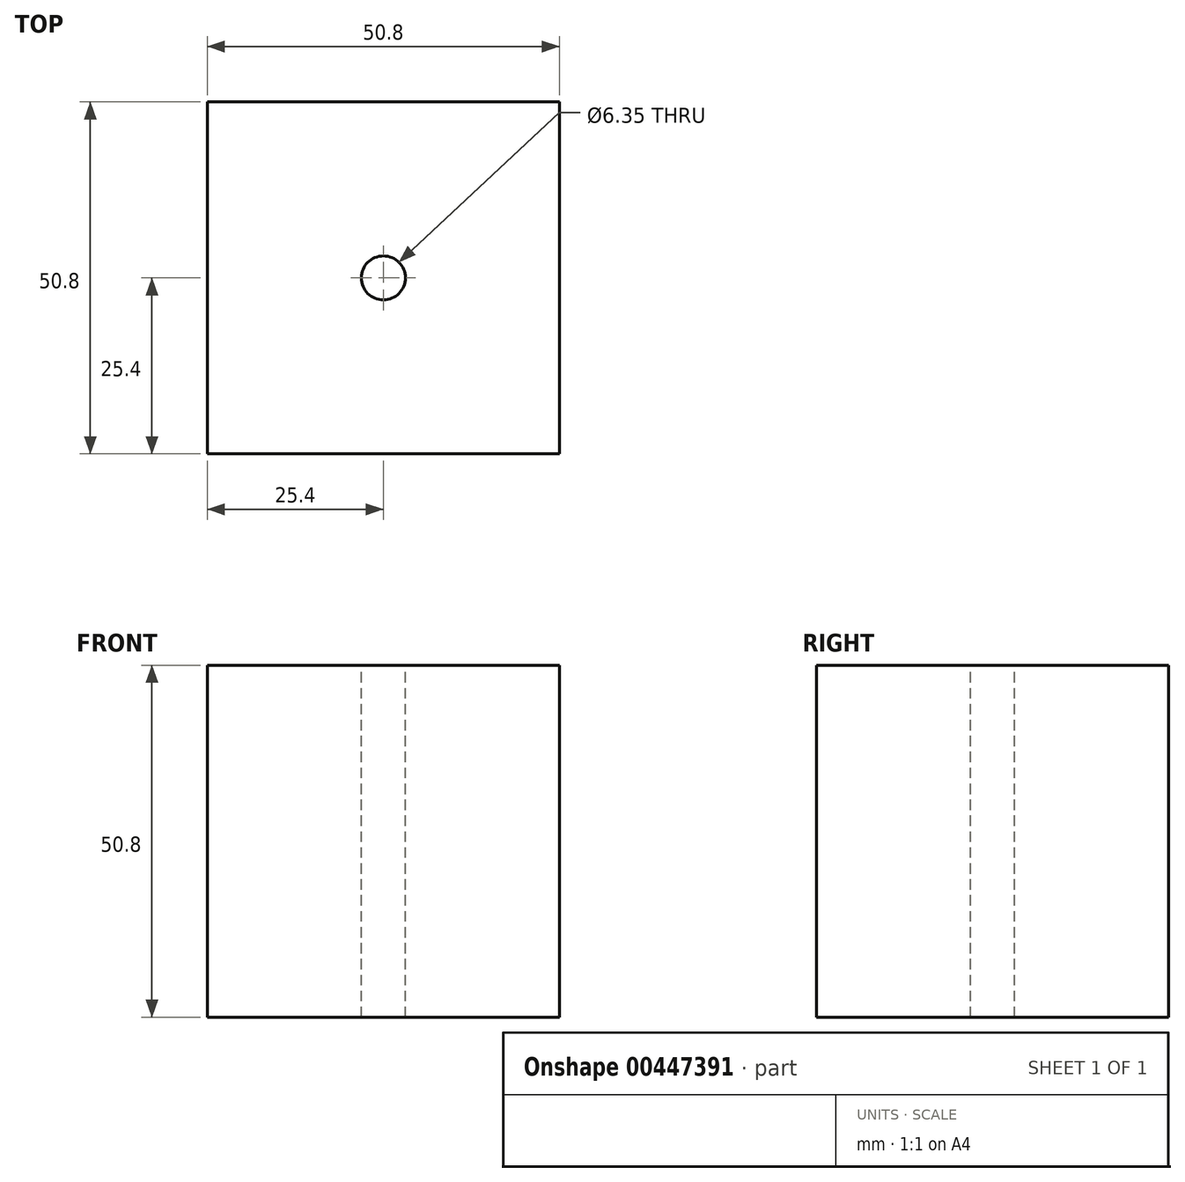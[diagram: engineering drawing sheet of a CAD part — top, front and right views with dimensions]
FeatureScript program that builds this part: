
annotation { "Feature Type Name" : "Feature", "Feature Type Description" : "" }
export const myFeature = defineFeature(function(context is Context, id is Id, definition is map)
    precondition{}
    {
        {
            var Q0;
            Q0=qCreatedBy(makeId("Front.planeOp"),FACE);
            var sketch = newSketch(context, id + "F0", { "sketchPlane" : qUnion([Q0])});
            skLineSegment(sketch, "E0.bottom", {"start": v(25.4, -25.4) * mm, "end": v(-25.4, -25.4) * mm});
            skLineSegment(sketch, "E0.top", {"start": v(25.4, 25.4) * mm, "end": v(-25.4, 25.4) * mm});
            skLineSegment(sketch, "E0.left", {"start": v(25.4, -25.4) * mm, "end": v(25.4, 25.4) * mm});
            skLineSegment(sketch, "E0.right", {"start": v(-25.4, -25.4) * mm, "end": v(-25.4, 25.4) * mm});
            skSolve(sketch);
        }
        {
            var Q0;
            Q0 = qSketchRegion(id + "F0", true);
            extrude(context, id + "F1", {"entities" : qUnion([Q0]), "endBound" : BoundingType.SYMMETRIC, "depth" : 50.8 * mm});
        }
        {
            var Q0;
            Q0=makeQuery(id+"F1.opExtrude","SWEPT_FACE",FACE,{"disambiguationData":[OSD([sQuery(id+"F0.wireOp",EDGE,"E0.top")])]});
            var sketch = newSketch(context, id + "F2", { "sketchPlane" : qUnion([Q0])});
            skCircle(sketch, "E1", {"center": v(0, 0) * mm, "radius": 15.96 * mm});
            skSolve(sketch);
        }
        {
            var Q0;
            Q0=sQuery(id+"F2.wireOp",VERTEX,"E1.center");
            var Q1;
            Q1=makeQuery(id+"F1.opExtrude","SWEPT_BODY",BODY,{"disambiguationData":[OSD([sQuery(id+"F0.wireOp",EDGE,"E0.bottom"),sQuery(id+"F0.wireOp",EDGE,"E0.top"),sQuery(id+"F0.wireOp",EDGE,"E0.left"),sQuery(id+"F0.wireOp",EDGE,"E0.right")])]});
            hole(context, id + "F3", {"style" : HoleStyle.SIMPLE, "endStyle" : HoleEndStyle.THROUGH, "holeDiameter" : 6.35 * mm, "isTappedThrough" : true, "tappedDepth" : 12.7 * mm, "tapClearance" : 3, "locations" : qUnion([Q0]), "scope" : qUnion([Q1])});
        }
    });
